FCSTD DOCUMENT  (FreeCAD 0.19R24276 (Git))
Label: Master_sketch
License: All rights reserved
LicenseURL: http://en.wikipedia.org/wiki/All_rights_reserved
objects: Sketcher::SketchObject×1, PartDesign::Body×1
note: 2 computed .brp shape members not serialized (recipe doc carries the construction recipe); baked Part::Feature solids carry a one-line shape summary decoded from their .brp

FEATURE [Sketcher::SketchObject] Sketch
  FullyConstrained = false
  MapMode = 5
  Support = -> [XY_Plane]
  sketch-geometry (8):
    g0: Circle CenterX=0 CenterY=0 CenterZ=0 NormalX=0 NormalY=0 NormalZ=1 AngleXU=0 Radius=34
    g1: Circle CenterX=0 CenterY=0 CenterZ=0 NormalX=0 NormalY=0 NormalZ=1 AngleXU=0 Radius=38.5
    g2: Circle CenterX=22.415 CenterY=0 CenterZ=0 NormalX=0 NormalY=0 NormalZ=1 AngleXU=0 Radius=11
    g3: Circle CenterX=22.415 CenterY=0 CenterZ=0 NormalX=0 NormalY=0 NormalZ=1 AngleXU=0 Radius=16
    g4: LineSegment StartX=0 StartY=0 StartZ=0 EndX=22.415 EndY=0 EndZ=0
    g5: Circle CenterX=-22.4093 CenterY=0 CenterZ=0 NormalX=0 NormalY=0 NormalZ=1 AngleXU=0 Radius=11
    g6: Circle CenterX=-22.4093 CenterY=0 CenterZ=0 NormalX=0 NormalY=0 NormalZ=1 AngleXU=0 Radius=16
    g7: LineSegment StartX=0 StartY=0 StartZ=0 EndX=-22.4093 EndY=0 EndZ=0
  constraints (16):
    c: Coincident(g0,g-1)
    c: Diameter(g0) = 68
    c: Coincident(g1,g0)
    c: Diameter(g1) = 77
    c: Coincident(g3,g2)
    c: Diameter(g3) = 32
    c: Diameter(g2) = 22
    c: Coincident(g4,g0)
    c: PointOnObject(g4,g-1)
    c: Coincident(g2,g4)
    c: Coincident(g6,g5)
    c: Equal(g3,g6) = 16
    c: Equal(g2,g5) = 12
    c: Coincident(g7,g0)
    c: PointOnObject(g7,g-1)
    c: Coincident(g5,g7)
FEATURE [PartDesign::Body] Body
  Group = -> [Sketch]
  Origin = -> Origin
